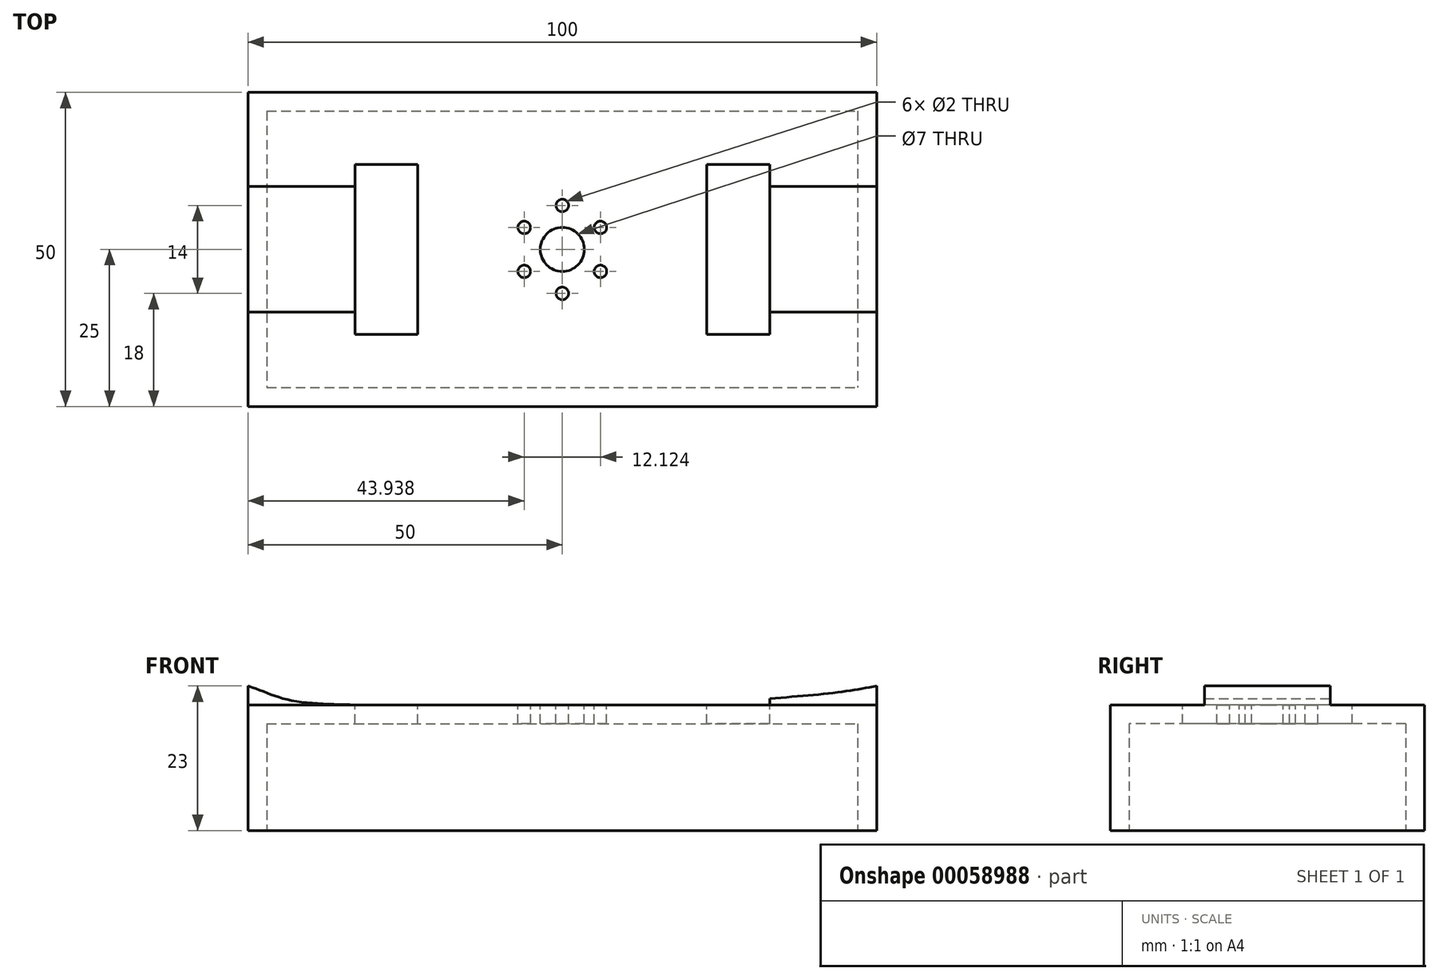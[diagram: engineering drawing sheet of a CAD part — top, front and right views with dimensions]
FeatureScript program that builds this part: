
annotation { "Feature Type Name" : "Feature", "Feature Type Description" : "" }
export const myFeature = defineFeature(function(context is Context, id is Id, definition is map)
    precondition{}
    {
        {
            var Q0;
            Q0=qCreatedBy(makeId("Top.planeOp"),FACE);
            var sketch = newSketch(context, id + "F0", { "sketchPlane" : qUnion([Q0])});
            skLineSegment(sketch, "E0.rect.bottom", {"start": v(-50, 25) * mm, "end": v(50, 25) * mm});
            skLineSegment(sketch, "E0.rect.top", {"start": v(-50, -25) * mm, "end": v(50, -25) * mm});
            skLineSegment(sketch, "E0.rect.left", {"start": v(-50, 25) * mm, "end": v(-50, -25) * mm});
            skLineSegment(sketch, "E0.rect.right", {"start": v(50, 25) * mm, "end": v(50, -25) * mm});
            skPoint(sketch, "E0.rect.middle", {"position": v(0, 0) * mm});
            skSolve(sketch);
        }
        {
            var Q0;
            Q0=makeQuery(id+"F0.imprint","IMPRINT",FACE,{"disambiguationData":[TD([[makeQuery(id+"F0.imprint","IMPRINT",EDGE,{"derivedFrom":sQuery(id+"F0.wireOp",EDGE,"E0.rect.bottom")}),-1.0]])]});
            extrude(context, id + "F1", {"entities" : qUnion([Q0]), "depth" : 20 * mm});
        }
        {
            var Q0;
            Q0=makeQuery(id+"F1.opExtrude","CAP_FACE",FACE,{"disambiguationData":[OSD([sQuery(id+"F0.wireOp",EDGE,"E0.rect.bottom"),sQuery(id+"F0.wireOp",EDGE,"E0.rect.top"),sQuery(id+"F0.wireOp",EDGE,"E0.rect.left"),sQuery(id+"F0.wireOp",EDGE,"E0.rect.right")])],"isStart":true});
            shell(context, id + "F2", {"entities" : qUnion([Q0]), "thickness" : 3 * mm});
        }
        {
            var Q0;
            Q0=makeQuery(id+"F1.opExtrude","CAP_FACE",FACE,{"disambiguationData":[OSD([sQuery(id+"F0.wireOp",EDGE,"E0.rect.bottom"),sQuery(id+"F0.wireOp",EDGE,"E0.rect.top"),sQuery(id+"F0.wireOp",EDGE,"E0.rect.left"),sQuery(id+"F0.wireOp",EDGE,"E0.rect.right")])],"isStart":false});
            var sketch = newSketch(context, id + "F3", { "sketchPlane" : qUnion([Q0])});
            skCircle(sketch, "E1", {"center": v(0, 0) * mm, "radius": 3.5 * mm});
            skCircle(sketch, "E2", {"center": v(0, 7) * mm, "radius": 1 * mm});
            skCircle(sketch, "E3.1.0", {"center": v(-6.06, 3.5) * mm, "radius": 1 * mm});
            skCircle(sketch, "E3.2.0", {"center": v(-6.06, -3.5) * mm, "radius": 1 * mm});
            skCircle(sketch, "E3.3.0", {"center": v(0, -7) * mm, "radius": 1 * mm});
            skCircle(sketch, "E3.4.0", {"center": v(6.06, -3.5) * mm, "radius": 1 * mm});
            skCircle(sketch, "E3.5.0", {"center": v(6.06, 3.5) * mm, "radius": 1 * mm});
            skLineSegment(sketch, "E4.rect.bottom", {"start": v(-33, 13.5) * mm, "end": v(-23, 13.5) * mm});
            skLineSegment(sketch, "E4.rect.top", {"start": v(-33, -13.5) * mm, "end": v(-23, -13.5) * mm});
            skLineSegment(sketch, "E4.rect.left", {"start": v(-33, 13.5) * mm, "end": v(-33, -13.5) * mm});
            skLineSegment(sketch, "E4.rect.right", {"start": v(-23, 13.5) * mm, "end": v(-23, -13.5) * mm});
            skPoint(sketch, "E4.rect.middle", {"position": v(-28, 0) * mm});
            skLineSegment(sketch, "E5.MirrorCS", {"start": v(33, 13.5) * mm, "end": v(23, 13.5) * mm});
            skLineSegment(sketch, "E6.MirrorCS", {"start": v(23, 13.5) * mm, "end": v(23, -13.5) * mm});
            skLineSegment(sketch, "E7.MirrorCS", {"start": v(33, 13.5) * mm, "end": v(33, -13.5) * mm});
            skLineSegment(sketch, "E8.MirrorCS", {"start": v(33, -13.5) * mm, "end": v(23, -13.5) * mm});
            skSolve(sketch);
        }
        {
            var Q0;
            Q0 = qSketchRegion(id + "F3", true);
            extrude(context, id + "F4", {"entities" : qUnion([Q0]), "operationType" : NewBodyOperationType.REMOVE, "oppositeDirection" : true, "depth" : 25 * mm});
        }
        {
            var Q0;
            Q0=qCreatedBy(makeId("Front.planeOp"),FACE);
            var sketch = newSketch(context, id + "F5", { "sketchPlane" : qUnion([Q0])});
            skLineSegment(sketch, "E9", {"start": v(50, 20) * mm, "end": v(50, 23) * mm});
            skLineSegment(sketch, "E10", {"start": v(33, 20) * mm, "end": v(50, 20) * mm});
            skLineSegment(sketch, "E11.MirrorCS", {"start": v(-50, 20) * mm, "end": v(-50, 23) * mm});
            skFitSpline(sketch, "E12.MirrorCS", {"points": [v(-50, 23) * mm, v(-43.65, 20.82) * mm, v(-33, 20) * mm], "startDerivative": vector(15.28, -4.58) * mm, "endDerivative": vector(17.79, -0.55) * mm});
            skLineSegment(sketch, "E13.MirrorCS", {"start": v(-33, 20) * mm, "end": v(-50, 20) * mm});
            skLineSegment(sketch, "E14", {"start": v(33, 20) * mm, "end": v(33, 21) * mm});
            skFitSpline(sketch, "E15", {"points": [v(33, 21) * mm, v(43.83, 22) * mm, v(50, 23) * mm], "startDerivative": vector(20.39, 1.6) * mm, "endDerivative": vector(13.29, 2.44) * mm});
            skSolve(sketch);
        }
        {
            var Q0;
            Q0 = qSketchRegion(id + "F5", true);
            extrude(context, id + "F6", {"entities" : qUnion([Q0]), "operationType" : NewBodyOperationType.ADD, "endBound" : BoundingType.SYMMETRIC, "depth" : 20 * mm});
        }
    });
